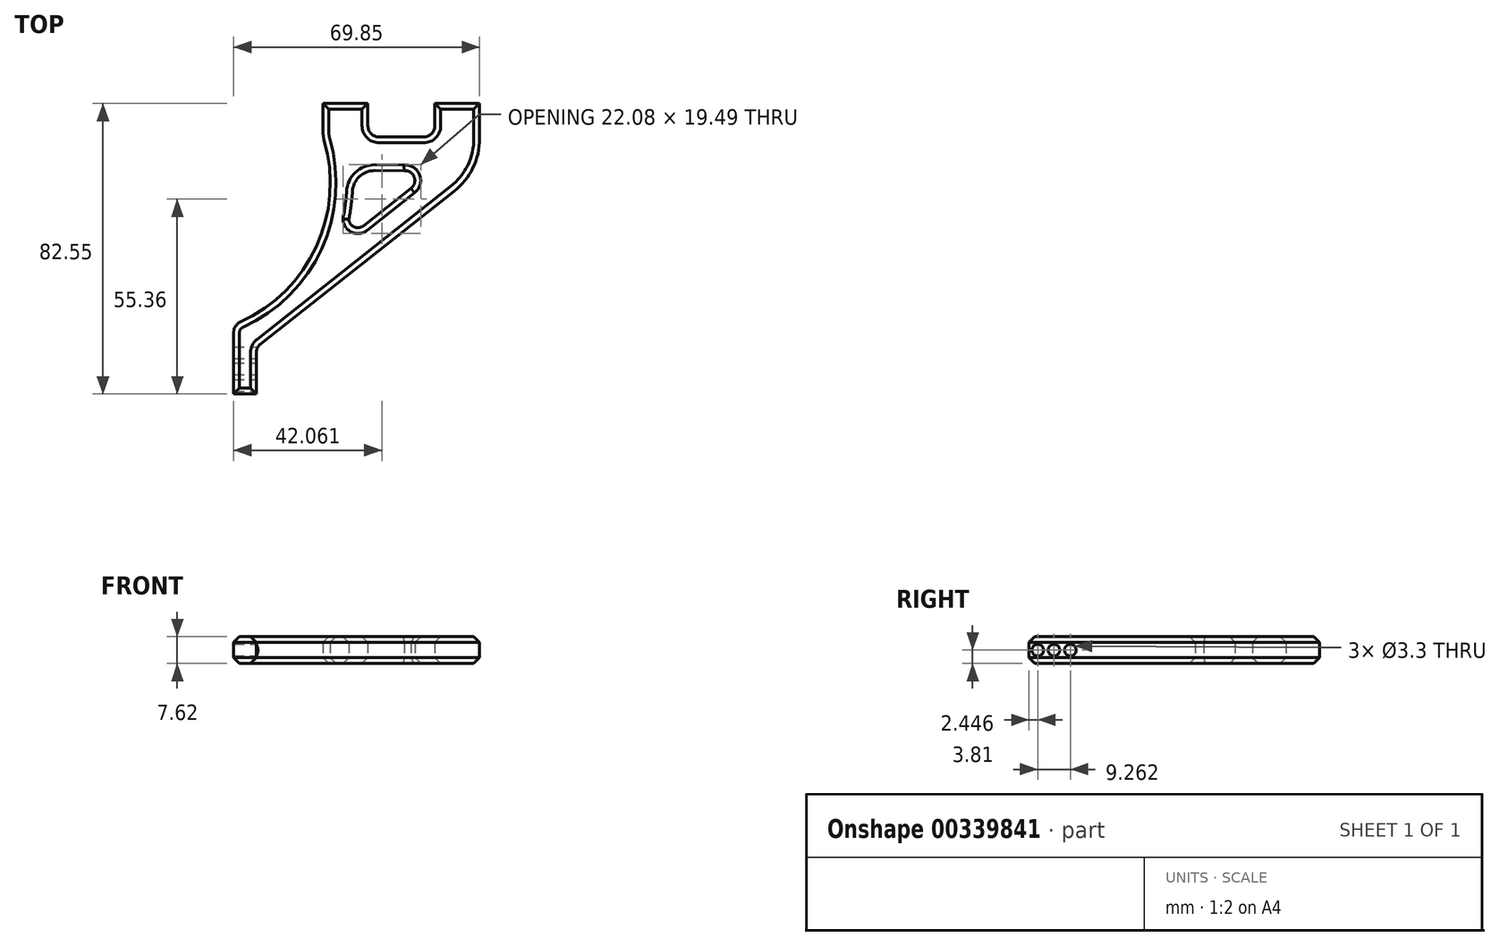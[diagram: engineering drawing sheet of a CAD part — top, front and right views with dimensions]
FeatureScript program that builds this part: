
annotation { "Feature Type Name" : "Feature", "Feature Type Description" : "" }
export const myFeature = defineFeature(function(context is Context, id is Id, definition is map)
    precondition{}
    {
        {
            var Q0;
            Q0=qCreatedBy(makeId("Top.planeOp"),FACE);
            var sketch = newSketch(context, id + "F0", { "sketchPlane" : qUnion([Q0])});
            skLineSegment(sketch, "E0", {"start": v(-21, 29.8) * mm, "end": v(-8.3, 29.8) * mm});
            skPoint(sketch, "E1", {"position": v(-21, -52.76) * mm});
            skPoint(sketch, "E2", {"position": v(-46.4, -52.76) * mm});
            skLineSegment(sketch, "E3", {"start": v(-46.4, -52.76) * mm, "end": v(-46.4, -39.5) * mm});
            skLineSegment(sketch, "E4", {"start": v(-39.96, -41.03) * mm, "end": v(-39.96, -52.76) * mm});
            skLineSegment(sketch, "E5", {"start": v(-39.96, -52.76) * mm, "end": v(-46.4, -52.76) * mm});
            skLineSegment(sketch, "E6", {"start": v(23.46, 29.8) * mm, "end": v(23.46, 19.78) * mm});
            skLineSegment(sketch, "E7", {"start": v(16.2, 4.83) * mm, "end": v(-38.75, -38.54) * mm});
            skLineSegment(sketch, "E8", {"start": v(-46.4, -39.5) * mm, "end": v(-46.4, -35.25) * mm});
            skLineSegment(sketch, "E9", {"start": v(-21, 29.8) * mm, "end": v(-21, 21.2) * mm});
            skArc(sketch, "E10", {"start": v(-44.52, -32.35) * mm, "mid": v(-22.95, -10.92) * mm, "end": v(-20.74, 19.42) * mm});
            skPoint(sketch, "E11", {"position": v(-8.3, 29.8) * mm});
            skPoint(sketch, "E12", {"position": v(10.76, 29.8) * mm});
            skPoint(sketch, "E13", {"position": v(-8.3, 20.27) * mm});
            skLineSegment(sketch, "E14", {"start": v(-8.3, 29.8) * mm, "end": v(-8.3, 23.44) * mm});
            skLineSegment(sketch, "E15", {"start": v(10.76, 23.44) * mm, "end": v(10.76, 29.8) * mm});
            skLineSegment(sketch, "E16", {"start": v(7.58, 20.27) * mm, "end": v(-5.12, 20.27) * mm});
            skArc(sketch, "E17.0", {"start": v(-13.71, -3.11) * mm, "mid": v(-13.05, 0.76) * mm, "end": v(-12.7, 4.67) * mm});
            skPoint(sketch, "E18", {"position": v(13.93, 10.55) * mm});
            skPoint(sketch, "E19", {"position": v(-8.3, 10.74) * mm});
            skPoint(sketch, "E20.end.orphan", {"position": v(-12.76, 10.74) * mm});
            skLineSegment(sketch, "E21", {"start": v(2.62, 10.63) * mm, "end": v(-6.3, 10.7) * mm});
            skLineSegment(sketch, "E22", {"start": v(4.07, 5.78) * mm, "end": v(-9.54, -4.97) * mm});
            skArc(sketch, "E23.filletArc", {"start": v(-6.3, 10.7) * mm, "mid": v(-10.71, 8.96) * mm, "end": v(-12.7, 4.67) * mm});
            skArc(sketch, "E24", {"start": v(3.78, 5.56) * mm, "mid": v(4.91, 8.79) * mm, "end": v(2.04, 10.64) * mm});
            skArc(sketch, "E25", {"start": v(-10.1, -5.3) * mm, "mid": v(-9.99, -5.24) * mm, "end": v(-9.87, -5.16) * mm});
            skLineSegment(sketch, "E26", {"start": v(-9.87, -5.16) * mm, "end": v(-9.54, -4.97) * mm});
            skArc(sketch, "E27", {"start": v(-13.71, -3.11) * mm, "mid": v(-12.19, -5.3) * mm, "end": v(-9.54, -4.97) * mm});
            skPoint(sketch, "E27.startSnap0", {"position": v(-13.62, -2.65) * mm});
            skPoint(sketch, "E28.orphan", {"position": v(-13.7, -3.06) * mm});
            skPoint(sketch, "E29.orphan", {"position": v(-13.7, -2.65) * mm});
            skPoint(sketch, "E30", {"position": v(3.78, 5.56) * mm});
            skPoint(sketch, "E31", {"position": v(2.04, 10.64) * mm});
            skArc(sketch, "E32.filletArc", {"start": v(-8.3, 23.44) * mm, "mid": v(-7.36, 21.2) * mm, "end": v(-5.12, 20.27) * mm});
            skPoint(sketch, "E33.visualSharp", {"position": v(10.76, 20.27) * mm});
            skArc(sketch, "E33.filletArc", {"start": v(7.58, 20.27) * mm, "mid": v(9.83, 21.2) * mm, "end": v(10.76, 23.44) * mm});
            skPoint(sketch, "E34.visualSharp", {"position": v(-39.96, -39.5) * mm});
            skArc(sketch, "E34.filletArc", {"start": v(-38.75, -38.54) * mm, "mid": v(-39.64, -39.65) * mm, "end": v(-39.96, -41.03) * mm});
            skPoint(sketch, "E35.visualSharp", {"position": v(-46.4, -33.14) * mm});
            skArc(sketch, "E35.filletArc", {"start": v(-44.52, -32.35) * mm, "mid": v(-45.88, -33.52) * mm, "end": v(-46.4, -35.25) * mm});
            skPoint(sketch, "E36.visualSharp", {"position": v(23.46, 10.55) * mm});
            skArc(sketch, "E36.filletArc", {"start": v(16.2, 4.83) * mm, "mid": v(21.55, 11.47) * mm, "end": v(23.46, 19.78) * mm});
            skPoint(sketch, "E37.visualSharp", {"position": v(-21, 20.26) * mm});
            skArc(sketch, "E37.filletArc", {"start": v(-21, 21.2) * mm, "mid": v(-20.93, 20.3) * mm, "end": v(-20.74, 19.42) * mm});
            skLineSegment(sketch, "E38.trimOffspring", {"start": v(10.76, 29.8) * mm, "end": v(23.46, 29.8) * mm});
            skSolve(sketch);
        }
        {
            var Q0;
            Q0=makeQuery(id+"F0.imprint","IMPRINT",FACE,{"disambiguationData":[TD([[makeQuery(id+"F0.imprint","IMPRINT",EDGE,{"derivedFrom":sQuery(id+"F0.wireOp",EDGE,"E0")}),-1.0]])]});
            extrude(context, id + "F1", {"entities" : qUnion([Q0]), "depth" : 7.62 * mm});
        }
        {
            var Q0;
            Q0=makeQuery(id+"F1.opExtrude","CAP_FACE",FACE,{"disambiguationData":[OSD([sQuery(id+"F0.wireOp",EDGE,"E0"),sQuery(id+"F0.wireOp",EDGE,"E3"),sQuery(id+"F0.wireOp",EDGE,"E4"),sQuery(id+"F0.wireOp",EDGE,"E5"),sQuery(id+"F0.wireOp",EDGE,"E6"),sQuery(id+"F0.wireOp",EDGE,"E7"),sQuery(id+"F0.wireOp",EDGE,"E8"),sQuery(id+"F0.wireOp",EDGE,"E9"),sQuery(id+"F0.wireOp",EDGE,"E10"),sQuery(id+"F0.wireOp",EDGE,"E14"),sQuery(id+"F0.wireOp",EDGE,"E15"),sQuery(id+"F0.wireOp",EDGE,"E16"),sQuery(id+"F0.wireOp",EDGE,"E17.0"),sQuery(id+"F0.wireOp",EDGE,"E21"),sQuery(id+"F0.wireOp",EDGE,"E22"),sQuery(id+"F0.wireOp",EDGE,"E23.filletArc"),sQuery(id+"F0.wireOp",EDGE,"E24"),sQuery(id+"F0.wireOp",EDGE,"E27"),sQuery(id+"F0.wireOp",EDGE,"E32.filletArc"),sQuery(id+"F0.wireOp",EDGE,"E33.filletArc"),sQuery(id+"F0.wireOp",EDGE,"E34.filletArc"),sQuery(id+"F0.wireOp",EDGE,"E35.filletArc"),sQuery(id+"F0.wireOp",EDGE,"E36.filletArc"),sQuery(id+"F0.wireOp",EDGE,"E37.filletArc"),sQuery(id+"F0.wireOp",EDGE,"E38.trimOffspring")])],"isStart":false});
            var Q1;
            Q1=makeQuery(id+"F1.opExtrude","CAP_FACE",FACE,{"disambiguationData":[OSD([sQuery(id+"F0.wireOp",EDGE,"E0"),sQuery(id+"F0.wireOp",EDGE,"E3"),sQuery(id+"F0.wireOp",EDGE,"E4"),sQuery(id+"F0.wireOp",EDGE,"E5"),sQuery(id+"F0.wireOp",EDGE,"E6"),sQuery(id+"F0.wireOp",EDGE,"E7"),sQuery(id+"F0.wireOp",EDGE,"E8"),sQuery(id+"F0.wireOp",EDGE,"E9"),sQuery(id+"F0.wireOp",EDGE,"E10"),sQuery(id+"F0.wireOp",EDGE,"E14"),sQuery(id+"F0.wireOp",EDGE,"E15"),sQuery(id+"F0.wireOp",EDGE,"E16"),sQuery(id+"F0.wireOp",EDGE,"E17.0"),sQuery(id+"F0.wireOp",EDGE,"E21"),sQuery(id+"F0.wireOp",EDGE,"E22"),sQuery(id+"F0.wireOp",EDGE,"E23.filletArc"),sQuery(id+"F0.wireOp",EDGE,"E24"),sQuery(id+"F0.wireOp",EDGE,"E27"),sQuery(id+"F0.wireOp",EDGE,"E32.filletArc"),sQuery(id+"F0.wireOp",EDGE,"E33.filletArc"),sQuery(id+"F0.wireOp",EDGE,"E34.filletArc"),sQuery(id+"F0.wireOp",EDGE,"E35.filletArc"),sQuery(id+"F0.wireOp",EDGE,"E36.filletArc"),sQuery(id+"F0.wireOp",EDGE,"E37.filletArc"),sQuery(id+"F0.wireOp",EDGE,"E38.trimOffspring")])],"isStart":true});
            chamfer(context, id + "F2", {"entities" : qUnion([Q0, Q1]), "width" : 1.65 * mm, "tangentPropagation" : true});
        }
        {
            var Q0;
            Q0=makeQuery(id+"F1.opExtrude","SWEPT_FACE",FACE,{"disambiguationData":[OSD([sQuery(id+"F0.wireOp",EDGE,"E3"),sQuery(id+"F0.wireOp",EDGE,"E8")])]});
            var sketch = newSketch(context, id + "F3", { "sketchPlane" : qUnion([Q0])});
            skCircle(sketch, "E39", {"center": v(50.31, 3.8) * mm, "radius": 1.45 * mm});
            skCircle(sketch, "E40", {"center": v(41.05, 3.81) * mm, "radius": 1.47 * mm});
            skPoint(sketch, "E41.trimOffspring.end.orphan", {"position": v(35.25, 3.81) * mm});
            skPoint(sketch, "E42.start.orphan", {"position": v(52.76, 3.81) * mm});
            skCircle(sketch, "E43", {"center": v(45.7, 3.81) * mm, "radius": 1.35 * mm});
            skLineSegment(sketch, "E44", {"start": v(35.25, 3.81) * mm, "end": v(52.76, 3.81) * mm});
            skSolve(sketch);
        }
        {
            var Q0;
            Q0=sQuery(id+"F3.wireOp",VERTEX,"E40.center");
            var Q1;
            Q1=sQuery(id+"F3.wireOp",VERTEX,"E43.center");
            var Q2;
            Q2=sQuery(id+"F3.wireOp",VERTEX,"E39.center");
            var Q3;
            Q3=makeQuery(id+"F1.opExtrude","SWEPT_BODY",BODY,{"disambiguationData":[OSD([sQuery(id+"F0.wireOp",EDGE,"E0"),sQuery(id+"F0.wireOp",EDGE,"E3"),sQuery(id+"F0.wireOp",EDGE,"E4"),sQuery(id+"F0.wireOp",EDGE,"E5"),sQuery(id+"F0.wireOp",EDGE,"E6"),sQuery(id+"F0.wireOp",EDGE,"E7"),sQuery(id+"F0.wireOp",EDGE,"E8"),sQuery(id+"F0.wireOp",EDGE,"E9"),sQuery(id+"F0.wireOp",EDGE,"E10"),sQuery(id+"F0.wireOp",EDGE,"E14"),sQuery(id+"F0.wireOp",EDGE,"E15"),sQuery(id+"F0.wireOp",EDGE,"E16"),sQuery(id+"F0.wireOp",EDGE,"E17.0"),sQuery(id+"F0.wireOp",EDGE,"E21"),sQuery(id+"F0.wireOp",EDGE,"E22"),sQuery(id+"F0.wireOp",EDGE,"E23.filletArc"),sQuery(id+"F0.wireOp",EDGE,"E24"),sQuery(id+"F0.wireOp",EDGE,"E27"),sQuery(id+"F0.wireOp",EDGE,"E32.filletArc"),sQuery(id+"F0.wireOp",EDGE,"E33.filletArc"),sQuery(id+"F0.wireOp",EDGE,"E34.filletArc"),sQuery(id+"F0.wireOp",EDGE,"E35.filletArc"),sQuery(id+"F0.wireOp",EDGE,"E36.filletArc"),sQuery(id+"F0.wireOp",EDGE,"E37.filletArc"),sQuery(id+"F0.wireOp",EDGE,"E38.trimOffspring")])]});
            hole(context, id + "F4", {"style" : HoleStyle.SIMPLE, "endStyle" : HoleEndStyle.THROUGH, "standardTappedOrClearance" : lookupTablePath({ "standard" : "ISO", "fit" : "Normal", "size" : "M3", "type" : "Clearance" }), "standardBlindInLast" : lookupTablePath({ "fit" : "Standard", "standard" : "ISO", "size" : "M3", "type" : "Clearance" }), "holeDiameter" : 3.3 * mm, "isTappedThrough" : true, "tappedDepth" : 12.7 * mm, "tapClearance" : 3, "locations" : qUnion([Q0, Q1, Q2]), "scope" : qUnion([Q3]), "startStyle" : HoleStartStyle.PART});
        }
    });
